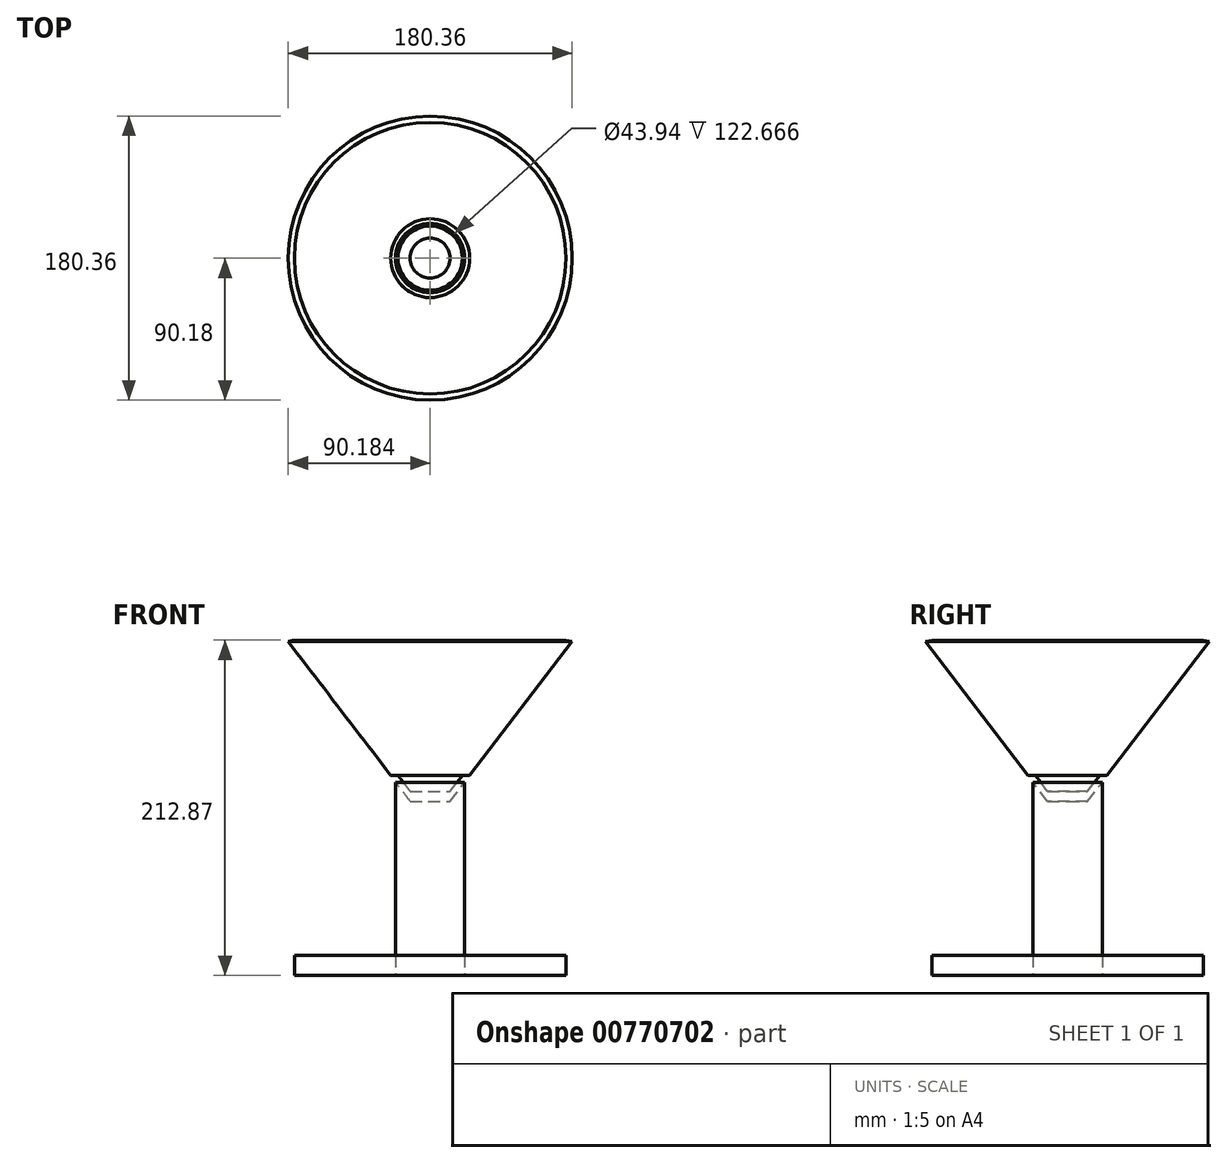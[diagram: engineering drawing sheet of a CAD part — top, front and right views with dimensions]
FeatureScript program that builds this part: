
annotation { "Feature Type Name" : "Feature", "Feature Type Description" : "" }
export const myFeature = defineFeature(function(context is Context, id is Id, definition is map)
    precondition{}
    {
        {
            var Q0;
            Q0=qCreatedBy(makeId("Front.planeOp"),FACE);
            var sketch = newSketch(context, id + "F0", { "sketchPlane" : qUnion([Q0])});
            skLineSegment(sketch, "E0", {"start": v(76.2, -86.72) * mm, "end": v(76.2, -74.02) * mm});
            skLineSegment(sketch, "E1", {"start": v(10.38, 40.28) * mm, "end": v(76.2, 126.15) * mm});
            skLineSegment(sketch, "E2", {"start": v(76.2, -86.72) * mm, "end": v(15, -86.72) * mm});
            skLineSegment(sketch, "E3", {"start": v(14.98, -74.02) * mm, "end": v(15.24, -74.02) * mm});
            skLineSegment(sketch, "E4", {"start": v(76.2, -74.02) * mm, "end": v(14.98, -74.02) * mm});
            skLineSegment(sketch, "E5", {"start": v(15, 40.28) * mm, "end": v(80.13, 125.25) * mm});
            skLineSegment(sketch, "E6", {"start": v(80.13, 125.25) * mm, "end": v(76.2, 126.15) * mm});
            skLineSegment(sketch, "E7", {"start": v(10.38, 40.28) * mm, "end": v(2.65, 30.2) * mm});
            skLineSegment(sketch, "E8", {"start": v(2.65, 30.2) * mm, "end": v(2.65, 23.85) * mm});
            skLineSegment(sketch, "E9", {"start": v(2.65, 23.85) * mm, "end": v(11.93, 35.94) * mm});
            skLineSegment(sketch, "E10", {"start": v(15, -86.72) * mm, "end": v(15, 40.28) * mm});
            skLineSegment(sketch, "E11", {"start": v(11.93, 35.94) * mm, "end": v(11.93, -86.72) * mm});
            skLineSegment(sketch, "E12", {"start": v(11.93, -86.72) * mm, "end": v(15, -86.72) * mm});
            skLineSegment(sketch, "E13", {"start": v(15.24, -74.02) * mm, "end": v(-10.05, -74.02) * mm});
            skLineSegment(sketch, "E14", {"start": v(11.93, -86.72) * mm, "end": v(-10.05, -86.72) * mm});
            skLineSegment(sketch, "E15", {"start": v(-10.05, -86.72) * mm, "end": v(-10.05, -74.02) * mm});
            skSolve(sketch);
        }
        {
            var Q0;
            Q0=makeQuery(id+"F0.imprint","IMPRINT",FACE,{"disambiguationData":[TD([[makeQuery(id+"F0.imprint","IMPRINT",EDGE,{"derivedFrom":sQuery(id+"F0.wireOp",EDGE,"E0")}),1.0]])]});
            var Q1;
            {var subQ0=sQuery(id+"F0.wireOp",EDGE,"E14");Q1=makeQuery(id+"F0.imprint","IMPRINT",FACE,{"disambiguationData":[TD([[makeQuery(id+"F0.imprint","IMPRINT",EDGE,{"derivedFrom":subQ0}),-1.0]])]});}
            var Q2;
            Q2=makeQuery(id+"F0.imprint","IMPRINT",FACE,{"disambiguationData":[TD([[makeQuery(id+"F0.imprint","IMPRINT",EDGE,{"derivedFrom":sQuery(id+"F0.wireOp",EDGE,"E1")}),-1.0]])]});
            var Q3;
            Q3 = qSketchRegion(id + "F2", true);
            var Q4;
            Q4=sQuery(id+"F0.wireOp",EDGE,"E4");
            var Q5;
            Q5=sQuery(id+"F0.wireOp",EDGE,"E0");
            var Q6;
            Q6=sQuery(id+"F0.wireOp",EDGE,"E12");
            var Q7;
            Q7=sQuery(id+"F0.wireOp",EDGE,"E6");
            var Q8;
            Q8=sQuery(id+"F0.wireOp",EDGE,"E11");
            var Q9;
            Q9=sQuery(id+"F0.wireOp",EDGE,"E5");
            var Q10;
            Q10=sQuery(id+"F0.wireOp",EDGE,"E9");
            var Q11;
            Q11=sQuery(id+"F0.wireOp",EDGE,"E7");
            var Q12;
            Q12=sQuery(id+"F0.wireOp",EDGE,"E15");
            revolve(context, id + "F1", {"bodyType" : ToolBodyType.SURFACE, "operationType" : NewBodyOperationType.INTERSECT, "surfaceOperationType" : NewSurfaceOperationType.NEW, "entities" : qUnion([Q0, Q1, Q2, Q3]), "surfaceEntities" : qUnion([Q4, Q5, Q6, Q7, Q8, Q9, Q10, Q11]), "axis" : qUnion([Q12]), "revolveType" : RevolveType.FULL, "oppositeDirection" : true});
        }
    });
